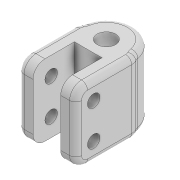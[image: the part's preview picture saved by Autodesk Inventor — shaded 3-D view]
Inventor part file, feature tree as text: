
AUTODESK INVENTOR PART (.ipt)
format: ipt  version: 2022 (Build 260153000, 153)  size: 214,016 bytes
history: native  units: mm
features: extrude x4, sketch x3, fillet x3
ambient origin geometry x8: Origin, YZ Plane, XZ Plane, XY Plane, X Axis, Y Axis, Z Axis, Center Point
bodies: Solid1 (feature_tree)
feature tree (10):
  extrude  "Extrusion1"  Depth=9.0mm
  sketch  "Sketch2"  dims[d2=12.0mm d3=0.0mm d4=4.65mm]
  extrude  "Extrusion2"  Depth=4.65mm
  extrude  "Extrusion4"  Depth=2.5mm
  extrude  "Extrusion3"  Depth=2.5mm
  fillet  "Fillet2"  Radius=10.0mm
  fillet  "Fillet3"  Radius=12.0mm
  fillet  "Fillet4"  Radius=2.1mm
  sketch  "Sketch1"  dims[d0=3.1mm d1=9.0mm]
  sketch  "Sketch3"  dims[d5=2.325mm d6=2.5mm d7=2.5mm d8=10.0mm d9=12.0mm d10=0.0mm d11=2.1mm d12=2.1mm d13=2.0mm d14=2.0mm d17=11.0mm d18=0.0mm d20=2.0mm d21=2.0mm d22=1.0mm d23=20.0mm d24=0.0mm d25=1.5mm d26=5.9mm d27=3.05mm]
